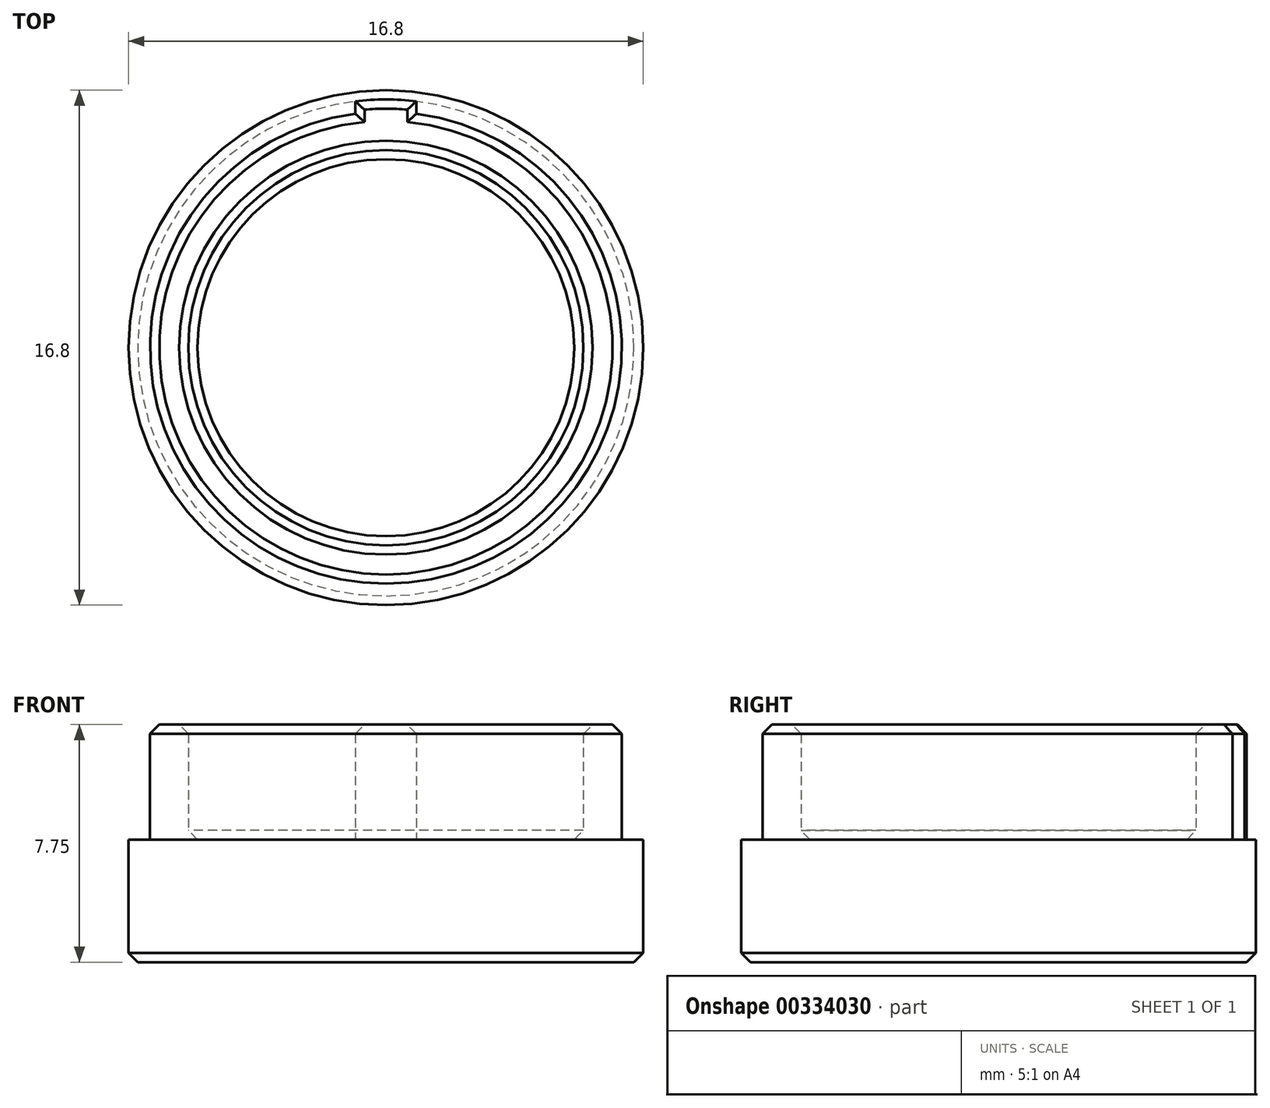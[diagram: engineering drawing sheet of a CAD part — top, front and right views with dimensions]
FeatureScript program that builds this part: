
annotation { "Feature Type Name" : "Feature", "Feature Type Description" : "" }
export const myFeature = defineFeature(function(context is Context, id is Id, definition is map)
    precondition{}
    {
        {
            var Q0;
            Q0=qCreatedBy(makeId("Top.planeOp"),FACE);
            var sketch = newSketch(context, id + "F0", { "sketchPlane" : qUnion([Q0])});
            skCircle(sketch, "E0", {"center": v(0, 0) * mm, "radius": 8.4 * mm});
            skSolve(sketch);
        }
        {
            var Q0;
            Q0 = qSketchRegion(id + "F0", true);
            extrude(context, id + "F1", {"entities" : qUnion([Q0]), "depth" : 4 * mm});
        }
        {
            var Q0;
            Q0=makeQuery(id+"F1.opExtrude","CAP_FACE",FACE,{"disambiguationData":[OSD([sQuery(id+"F0.wireOp",EDGE,"E0")])],"isStart":false});
            var sketch = newSketch(context, id + "F2", { "sketchPlane" : qUnion([Q0])});
            skCircle(sketch, "E1", {"center": v(0, 0) * mm, "radius": 7.7 * mm});
            skCircle(sketch, "E2", {"center": v(0, 0) * mm, "radius": 6.45 * mm});
            skSolve(sketch);
        }
        {
            var Q0;
            Q0 = qSketchRegion(id + "F2", true);
            extrude(context, id + "F3", {"entities" : qUnion([Q0]), "operationType" : NewBodyOperationType.ADD, "depth" : 3.75 * mm});
        }
        {
            var Q0;
            {var subQ0=sQuery(id+"F0.wireOp",EDGE,"E0");Q0=makeQuery(id+"F3.boolean.opBoolean","SPLIT",FACE,{"disambiguationData":[TD([makeQuery(id+"F1.opExtrude","SWEPT_FACE",FACE,{"disambiguationData":[OSD([subQ0])]})])],"derivedFrom":makeQuery(id+"F1.opExtrude","CAP_FACE",FACE,{"disambiguationData":[OSD([subQ0])],"isStart":false})});}
            var sketch = newSketch(context, id + "F4", { "sketchPlane" : qUnion([Q0])});
            skLineSegment(sketch, "E3", {"start": v(0, 0) * mm, "end": v(0, 8.1) * mm, "construction": true});
            skArc(sketch, "E4", {"start": v(1, 8.04) * mm, "mid": v(0, 8.1) * mm, "end": v(-1, 8.04) * mm});
            skLineSegment(sketch, "E5", {"start": v(-1, 8.04) * mm, "end": v(1, 8.04) * mm, "construction": true});
            skArc(sketch, "E6.0", {"start": v(1, 7.63) * mm, "mid": v(0, 7.7) * mm, "end": v(-1, 7.63) * mm});
            skLineSegment(sketch, "E7", {"start": v(-1, 8.04) * mm, "end": v(-1, 7.63) * mm});
            skLineSegment(sketch, "E8", {"start": v(1, 8.04) * mm, "end": v(1, 7.63) * mm});
            skSolve(sketch);
        }
        {
            var Q0;
            Q0 = qSketchRegion(id + "F4", true);
            var Q1;
            Q1=makeQuery(id+"F3.opExtrude","CAP_FACE",FACE,{"disambiguationData":[OSD([sQuery(id+"F2.wireOp",EDGE,"E1"),sQuery(id+"F2.wireOp",EDGE,"E2")])],"isStart":false});
            extrude(context, id + "F5", {"entities" : qUnion([Q0]), "operationType" : NewBodyOperationType.ADD, "endBound" : BoundingType.UP_TO_SURFACE, "endBoundEntityFace" : qUnion([Q1]), "depth" : 3.75 * mm});
        }
        {
            var Q0;
            Q0=qCreatedBy(makeId("Front.planeOp"),FACE);
            var sketch = newSketch(context, id + "F6", { "sketchPlane" : qUnion([Q0])});
            skLineSegment(sketch, "E9", {"start": v(0, 0) * mm, "end": v(0, 9.34) * mm, "construction": true});
            skSolve(sketch);
        }
        {
            var Q0;
            Q0=makeQuery(id+"F1.opExtrude","CAP_EDGE",EDGE,{"disambiguationData":[OSD([sQuery(id+"F0.wireOp",EDGE,"E0")])],"isStart":true});
            var Q1;
            {var subQ0=sQuery(id+"F4.wireOp",EDGE,"E8");var subQ1=sQuery(id+"F4.wireOp",EDGE,"E7");var subQ2=sQuery(id+"F4.wireOp",EDGE,"E6.0");var subQ3=sQuery(id+"F4.wireOp",EDGE,"E4");Q1=makeQuery(id+"FlG4vRh9ghELuDp_1.7.F5.boolean.opBoolean","MERGE",FACE,{"derivedFrom":[makeQuery(id+"FlG4vRh9ghELuDp_1.6.F5.boolean.opBoolean","MERGE",FACE,{"derivedFrom":[makeQuery(id+"FlG4vRh9ghELuDp_1.5.F5.boolean.opBoolean","MERGE",FACE,{"derivedFrom":[makeQuery(id+"FlG4vRh9ghELuDp_1.4.F5.boolean.opBoolean","MERGE",FACE,{"derivedFrom":[makeQuery(id+"FlG4vRh9ghELuDp_1.3.F5.boolean.opBoolean","MERGE",FACE,{"derivedFrom":[makeQuery(id+"FlG4vRh9ghELuDp_1.2.F5.boolean.opBoolean","MERGE",FACE,{"derivedFrom":[makeQuery(id+"FlG4vRh9ghELuDp_1.1.F5.boolean.opBoolean","MERGE",FACE,{"derivedFrom":[makeQuery(id+"F5.boolean.opBoolean","MERGE",FACE,{"derivedFrom":[makeQuery(id+"F3.opExtrude","CAP_FACE",FACE,{"disambiguationData":[OSD([sQuery(id+"F2.wireOp",EDGE,"E1"),sQuery(id+"F2.wireOp",EDGE,"E2")])],"isStart":false}),makeQuery(id+"F5.opExtrude","CAP_FACE",FACE,{"disambiguationData":[OSD([subQ3,subQ2,subQ1,subQ0])],"isStart":false})]}),makeQuery(id+"FlG4vRh9ghELuDp_1.1.F5.opExtrude","CAP_FACE",FACE,{"disambiguationData":[OSD([subQ3,subQ2,subQ1,subQ0])],"isStart":false})]}),makeQuery(id+"FlG4vRh9ghELuDp_1.2.F5.opExtrude","CAP_FACE",FACE,{"disambiguationData":[OSD([subQ3,subQ2,subQ1,subQ0])],"isStart":false})]}),makeQuery(id+"FlG4vRh9ghELuDp_1.3.F5.opExtrude","CAP_FACE",FACE,{"disambiguationData":[OSD([subQ3,subQ2,subQ1,subQ0])],"isStart":false})]}),makeQuery(id+"FlG4vRh9ghELuDp_1.4.F5.opExtrude","CAP_FACE",FACE,{"disambiguationData":[OSD([subQ3,subQ2,subQ1,subQ0])],"isStart":false})]}),makeQuery(id+"FlG4vRh9ghELuDp_1.5.F5.opExtrude","CAP_FACE",FACE,{"disambiguationData":[OSD([subQ3,subQ2,subQ1,subQ0])],"isStart":false})]}),makeQuery(id+"FlG4vRh9ghELuDp_1.6.F5.opExtrude","CAP_FACE",FACE,{"disambiguationData":[OSD([subQ3,subQ2,subQ1,subQ0])],"isStart":false})]}),makeQuery(id+"FlG4vRh9ghELuDp_1.7.F5.opExtrude","CAP_FACE",FACE,{"disambiguationData":[OSD([subQ3,subQ2,subQ1,subQ0])],"isStart":false})]});}
            var Q2;
            Q2=makeQuery(id+"F3.opExtrude","CAP_EDGE",EDGE,{"disambiguationData":[OSD([sQuery(id+"F2.wireOp",EDGE,"E2")])],"isStart":true});
            chamfer(context, id + "F7", {"entities" : qUnion([Q0, Q1, Q2]), "width" : 0.3 * mm, "tangentPropagation" : true});
        }
    });
